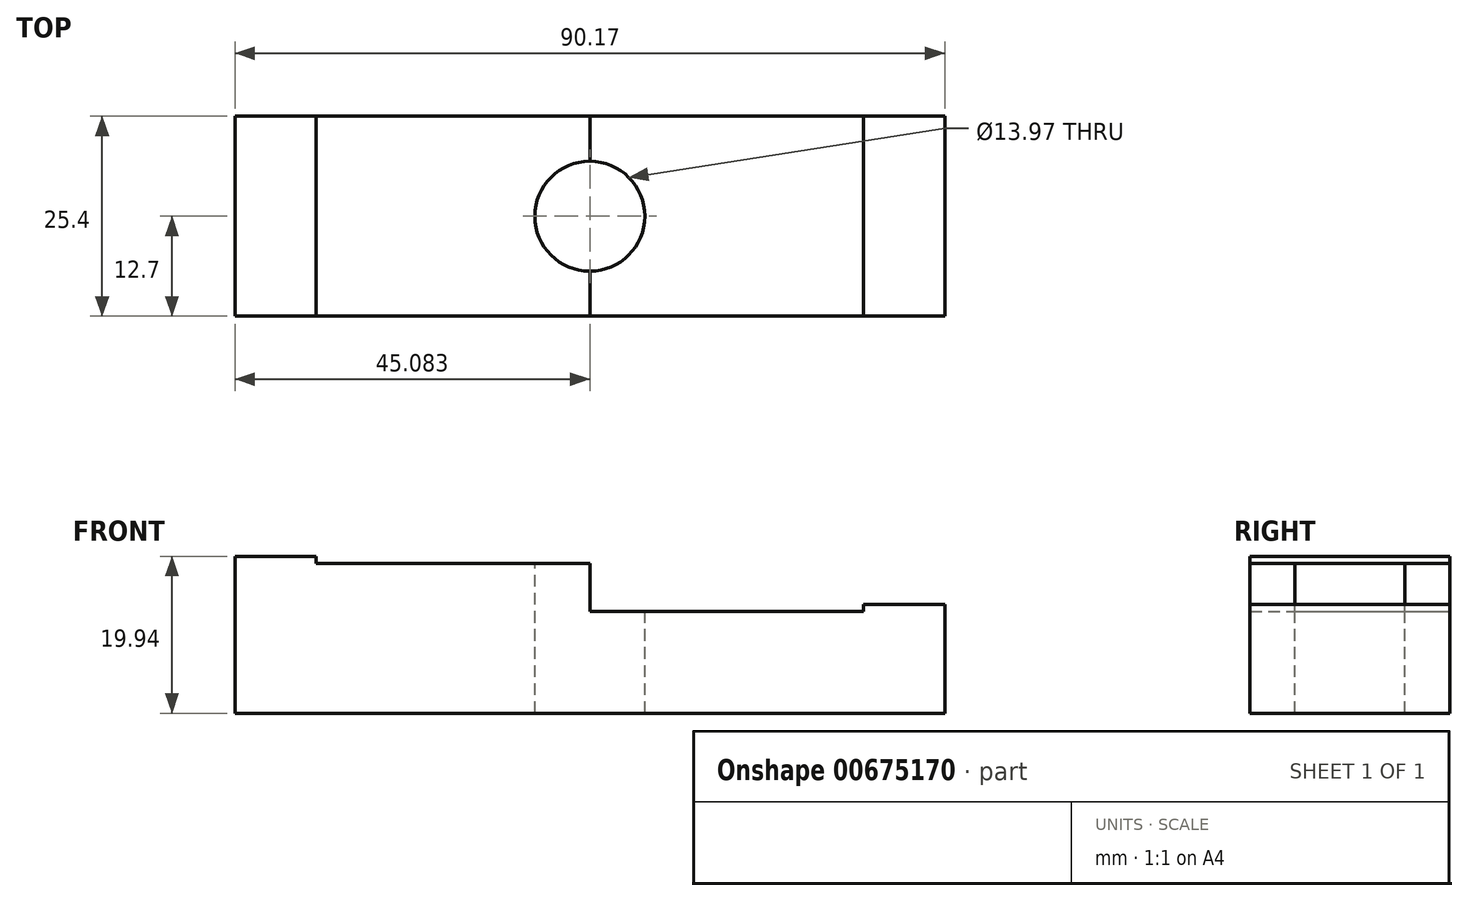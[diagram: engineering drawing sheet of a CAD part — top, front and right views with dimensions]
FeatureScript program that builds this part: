
annotation { "Feature Type Name" : "Feature", "Feature Type Description" : "" }
export const myFeature = defineFeature(function(context is Context, id is Id, definition is map)
    precondition{}
    {
        {
            var Q0;
            Q0=qCreatedBy(makeId("Front.planeOp"),FACE);
            var sketch = newSketch(context, id + "F0", { "sketchPlane" : qUnion([Q0])});
            skLineSegment(sketch, "E0.bottom", {"start": v(-45.08, 12.74) * mm, "end": v(-34.76, 12.74) * mm});
            skLineSegment(sketch, "E0.top", {"start": v(-45.08, -7.2) * mm, "end": v(45.09, -7.2) * mm});
            skLineSegment(sketch, "E0.left", {"start": v(-45.08, 12.74) * mm, "end": v(-45.08, -7.2) * mm});
            skLineSegment(sketch, "E0.right", {"start": v(45.09, 5.76) * mm, "end": v(45.09, -7.2) * mm});
            skLineSegment(sketch, "E1.top", {"start": v(-34.76, 11.85) * mm, "end": v(0, 11.85) * mm});
            skLineSegment(sketch, "E1.left", {"start": v(-34.76, 12.74) * mm, "end": v(-34.76, 11.85) * mm});
            skLineSegment(sketch, "E2.top", {"start": v(0, 5.76) * mm, "end": v(34.77, 5.76) * mm});
            skLineSegment(sketch, "E2.left", {"start": v(0, 11.85) * mm, "end": v(0, 5.76) * mm});
            skLineSegment(sketch, "E3.bottom", {"start": v(34.77, 6.65) * mm, "end": v(45.09, 6.65) * mm});
            skLineSegment(sketch, "E3.left", {"start": v(34.77, 6.65) * mm, "end": v(34.77, 5.76) * mm});
            skLineSegment(sketch, "E3.right", {"start": v(45.09, 6.65) * mm, "end": v(45.09, 5.76) * mm});
            skSolve(sketch);
        }
        {
            var Q0;
            Q0 = qSketchRegion(id + "F0", true);
            extrude(context, id + "F1", {"entities" : qUnion([Q0]), "depth" : 25.4 * mm, "offsetDistance" : 25.4 * mm});
        }
        {
            var Q0;
            Q0=makeQuery(id+"F1.opExtrude","SWEPT_FACE",FACE,{"disambiguationData":[OSD([sQuery(id+"F0.wireOp",EDGE,"E1.top")])]});
            var sketch = newSketch(context, id + "F2", { "sketchPlane" : qUnion([Q0])});
            skCircle(sketch, "E4", {"center": v(0, -12.7) * mm, "radius": 6.99 * mm});
            skSolve(sketch);
        }
        {
            var Q0;
            Q0 = qSketchRegion(id + "F2", true);
            extrude(context, id + "F3", {"entities" : qUnion([Q0]), "operationType" : NewBodyOperationType.REMOVE, "oppositeDirection" : true, "depth" : 25.4 * mm, "offsetDistance" : 25.4 * mm});
        }
    });
